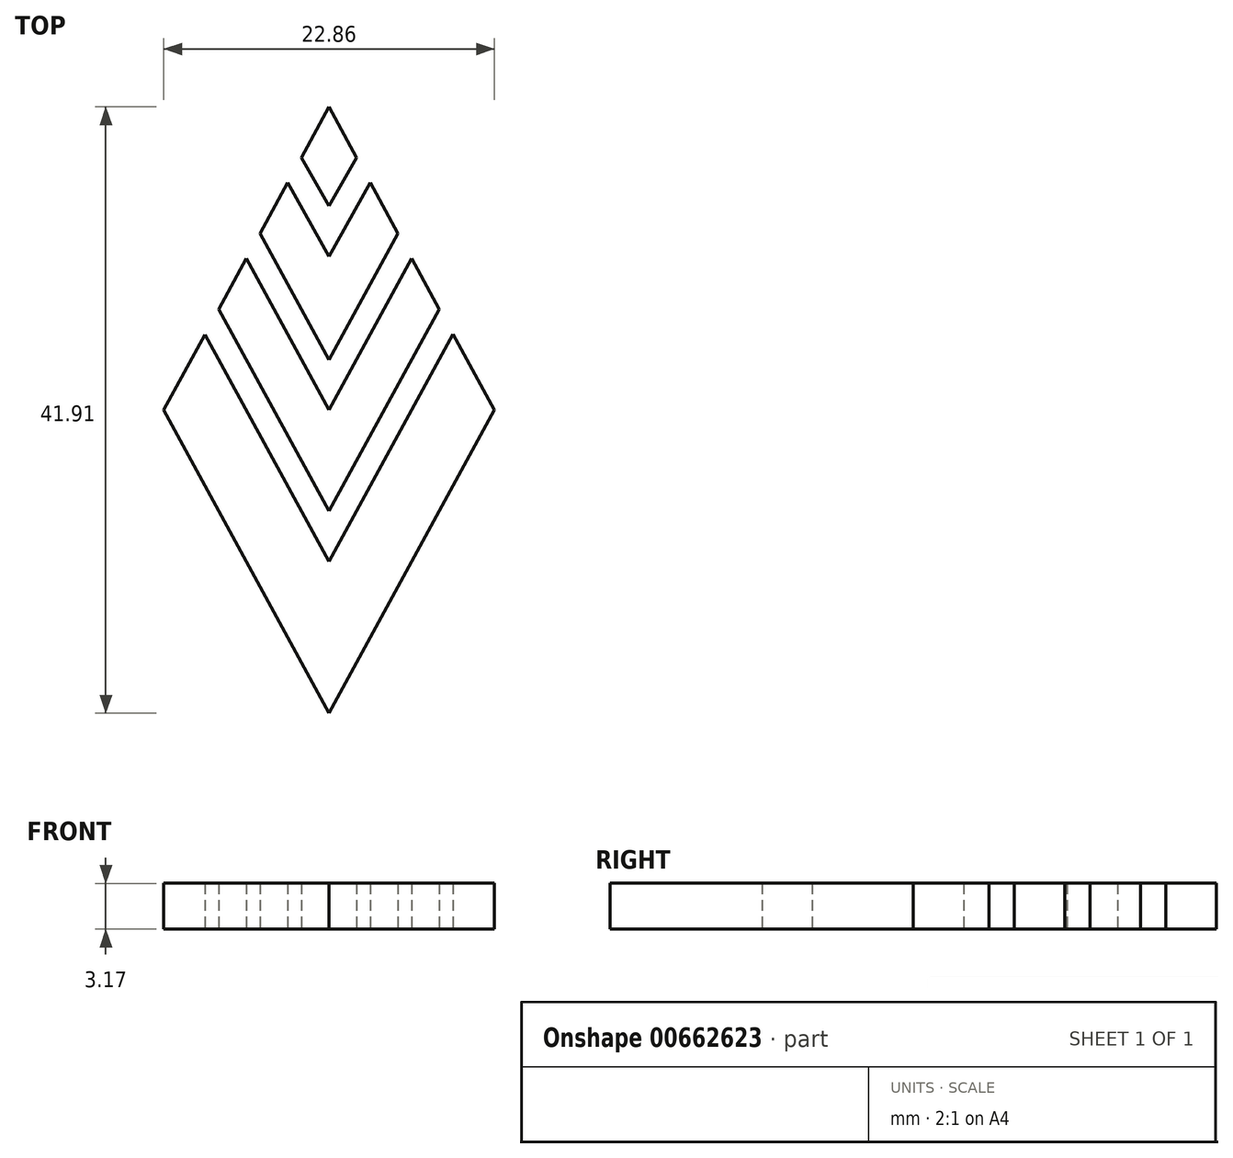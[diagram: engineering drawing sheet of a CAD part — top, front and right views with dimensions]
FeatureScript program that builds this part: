
annotation { "Feature Type Name" : "Feature", "Feature Type Description" : "" }
export const myFeature = defineFeature(function(context is Context, id is Id, definition is map)
    precondition{}
    {
        {
            var Q0;
            Q0=qCreatedBy(makeId("Top.planeOp"),FACE);
            var sketch = newSketch(context, id + "F0", { "sketchPlane" : qUnion([Q0])});
            skLineSegment(sketch, "E0", {"start": v(0, 41.91) * mm, "end": v(-1.9, 38.4) * mm});
            skLineSegment(sketch, "E1", {"start": v(-11.43, 20.96) * mm, "end": v(0, 0) * mm});
            skLineSegment(sketch, "E2", {"start": v(11.43, 20.96) * mm, "end": v(0, 0) * mm});
            skLineSegment(sketch, "E3", {"start": v(0, 41.91) * mm, "end": v(1.9, 38.4) * mm});
            skLineSegment(sketch, "E4", {"start": v(-1.9, 38.4) * mm, "end": v(0, 35.07) * mm});
            skLineSegment(sketch, "E5", {"start": v(1.9, 38.4) * mm, "end": v(0, 35.07) * mm});
            skLineSegment(sketch, "E6", {"start": v(-4.77, 33.17) * mm, "end": v(0, 24.44) * mm});
            skLineSegment(sketch, "E7", {"start": v(4.77, 33.17) * mm, "end": v(0, 24.44) * mm});
            skLineSegment(sketch, "E8", {"start": v(-7.63, 27.93) * mm, "end": v(0, 13.97) * mm});
            skLineSegment(sketch, "E9", {"start": v(7.63, 27.93) * mm, "end": v(0, 13.97) * mm});
            skLineSegment(sketch, "E10", {"start": v(-2.86, 36.67) * mm, "end": v(0, 31.59) * mm});
            skLineSegment(sketch, "E11", {"start": v(0, 31.59) * mm, "end": v(2.86, 36.67) * mm});
            skLineSegment(sketch, "E12", {"start": v(-5.72, 31.43) * mm, "end": v(0, 20.96) * mm});
            skLineSegment(sketch, "E13", {"start": v(0, 20.96) * mm, "end": v(5.71, 31.44) * mm});
            skLineSegment(sketch, "E14", {"start": v(-8.57, 26.19) * mm, "end": v(0, 10.5) * mm});
            skLineSegment(sketch, "E15", {"start": v(0, 10.5) * mm, "end": v(8.57, 26.2) * mm});
            skLineSegment(sketch, "E16.trimOffspring", {"start": v(-8.57, 26.19) * mm, "end": v(-11.43, 20.96) * mm});
            skLineSegment(sketch, "E17.trimOffspring", {"start": v(-5.72, 31.43) * mm, "end": v(-7.63, 27.93) * mm});
            skLineSegment(sketch, "E18.trimOffspring", {"start": v(-2.86, 36.67) * mm, "end": v(-4.77, 33.17) * mm});
            skLineSegment(sketch, "E19.trimOffspring", {"start": v(2.86, 36.67) * mm, "end": v(4.77, 33.17) * mm});
            skLineSegment(sketch, "E20.trimOffspring", {"start": v(5.71, 31.44) * mm, "end": v(7.63, 27.93) * mm});
            skLineSegment(sketch, "E21.trimOffspring", {"start": v(8.57, 26.2) * mm, "end": v(11.43, 20.95) * mm});
            skSolve(sketch);
        }
        {
            var Q0;
            Q0 = qSketchRegion(id + "F0", true);
            extrude(context, id + "F1", {"entities" : qUnion([Q0]), "depth" : 3.17 * mm, "offsetDistance" : 25.4 * mm});
        }
    });
